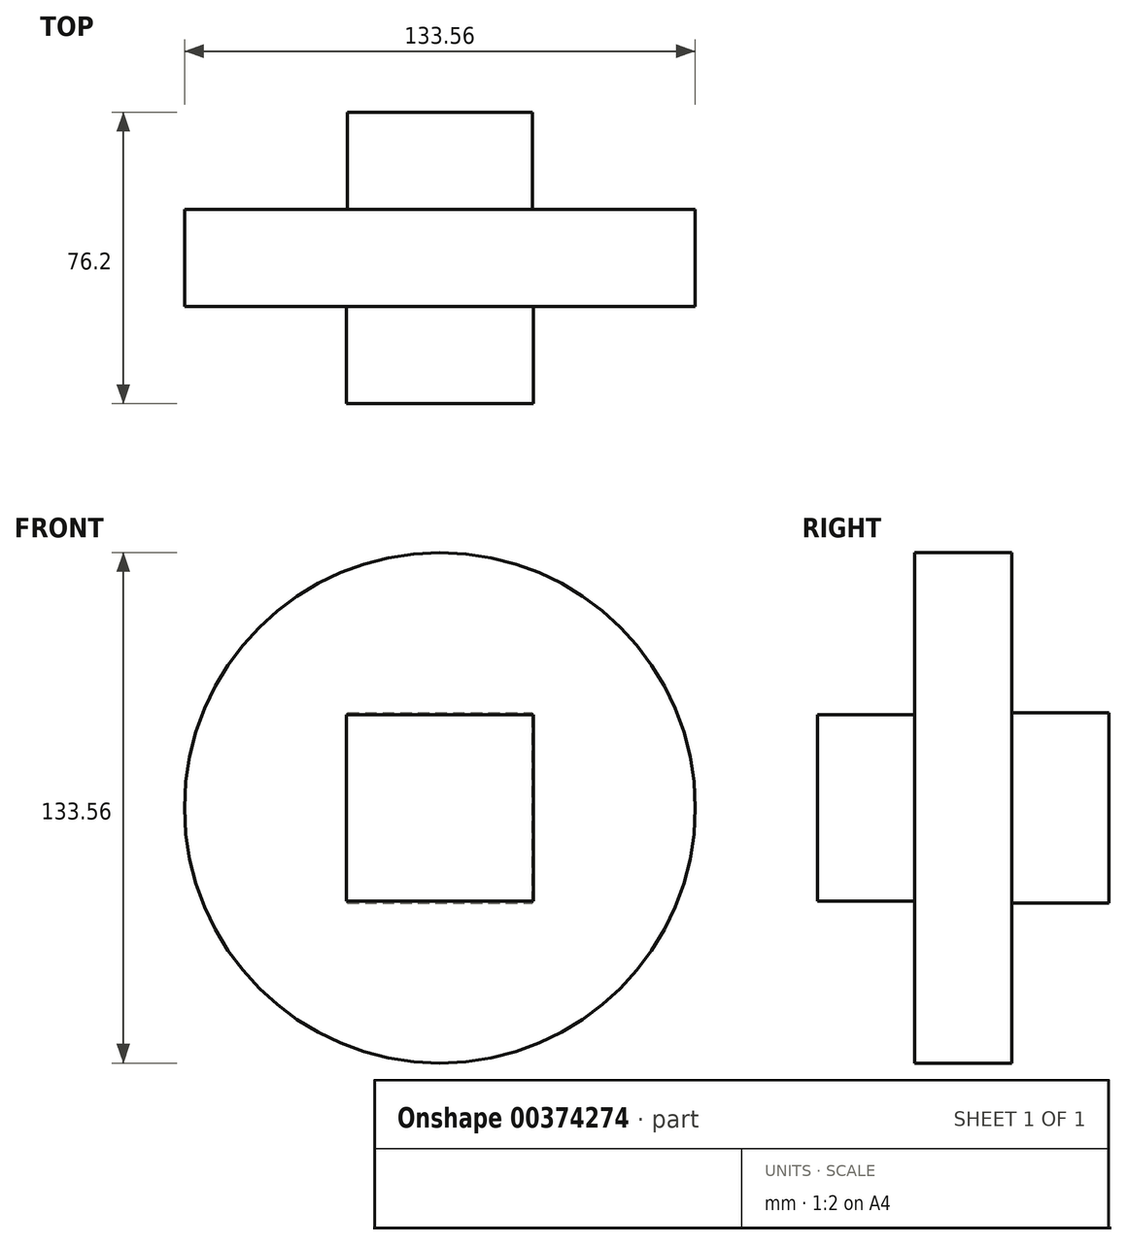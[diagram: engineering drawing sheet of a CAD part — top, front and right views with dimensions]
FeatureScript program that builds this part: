
annotation { "Feature Type Name" : "Feature", "Feature Type Description" : "" }
export const myFeature = defineFeature(function(context is Context, id is Id, definition is map)
    precondition{}
    {
        {
            var Q0;
            Q0=qCreatedBy(makeId("Front.planeOp"),FACE);
            var sketch = newSketch(context, id + "F0", { "sketchPlane" : qUnion([Q0])});
            skCircle(sketch, "E0", {"center": v(0, 0) * mm, "radius": 66.78 * mm});
            skLineSegment(sketch, "E1", {"start": v(0, 66.78) * mm, "end": v(-52.44, -41.35) * mm});
            skLineSegment(sketch, "E2", {"start": v(-52.44, -41.35) * mm, "end": v(0, 66.78) * mm});
            skLineSegment(sketch, "E3", {"start": v(0, 66.78) * mm, "end": v(51.62, -42.36) * mm});
            skLineSegment(sketch, "E4", {"start": v(51.62, -42.36) * mm, "end": v(-52.44, -41.35) * mm});
            skSolve(sketch);
        }
        {
            var Q0;
            Q0=qSketchRegion(id+"F0",true);
            extrude(context, id + "F1", {"entities" : qUnion([Q0]), "depth" : 25.4 * mm});
        }
        {
            var Q0;
            Q0=qCreatedBy(makeId("Front.planeOp"),FACE);
            var sketch = newSketch(context, id + "F2", { "sketchPlane" : qUnion([Q0])});
            skCircle(sketch, "E5", {"center": v(0, 0) * mm, "radius": 18.33 * mm});
            skCircle(sketch, "E6", {"center": v(0, 0) * mm, "radius": 35.86 * mm});
            skSolve(sketch);
        }
        {
            var Q0;
            Q0=qSketchRegion(id+"F2",true);
            extrude(context, id + "F3", {"entities" : qUnion([Q0]), "operationType" : NewBodyOperationType.REMOVE, "oppositeDirection" : true, "depth" : 25.4 * mm});
        }
        {
            var Q0;
            Q0=makeQuery(id+"F1.opExtrude","CAP_FACE",FACE,{"disambiguationData":[OSD([sQuery(id+"F0.wireOp",EDGE,"E0")])],"isStart":false});
            var sketch = newSketch(context, id + "F4", { "sketchPlane" : qUnion([Q0])});
            skLineSegment(sketch, "E7.bottom", {"start": v(24.42, -24.37) * mm, "end": v(-24.42, -24.37) * mm});
            skLineSegment(sketch, "E7.top", {"start": v(24.42, 24.37) * mm, "end": v(-24.42, 24.37) * mm});
            skLineSegment(sketch, "E7.left", {"start": v(24.42, -24.37) * mm, "end": v(24.42, 24.37) * mm});
            skLineSegment(sketch, "E7.right", {"start": v(-24.42, -24.37) * mm, "end": v(-24.42, 24.37) * mm});
            skPoint(sketch, "E7.middle", {"position": v(0, 0) * mm});
            skSolve(sketch);
        }
        {
            var Q0;
            Q0=makeQuery(id+"F4.imprint","IMPRINT",FACE,{"disambiguationData":[TD([[makeQuery(id+"F4.imprint","IMPRINT",EDGE,{"derivedFrom":sQuery(id+"F4.wireOp",EDGE,"E7.bottom")}),-1.0]])]});
            extrude(context, id + "F5", {"entities" : qUnion([Q0]), "operationType" : NewBodyOperationType.ADD, "depth" : 25.4 * mm});
        }
        {
            var Q0;
            Q0=makeQuery(id+"F1.opExtrude","CAP_FACE",FACE,{"disambiguationData":[OSD([sQuery(id+"F0.wireOp",EDGE,"E0")])],"isStart":true});
            var sketch = newSketch(context, id + "F6", { "sketchPlane" : qUnion([Q0])});
            skLineSegment(sketch, "E8.bottom", {"start": v(24.15, -24.9) * mm, "end": v(-24.15, -24.9) * mm});
            skLineSegment(sketch, "E8.top", {"start": v(24.15, 24.9) * mm, "end": v(-24.15, 24.9) * mm});
            skLineSegment(sketch, "E8.left", {"start": v(24.15, -24.9) * mm, "end": v(24.15, 24.9) * mm});
            skLineSegment(sketch, "E8.right", {"start": v(-24.15, -24.9) * mm, "end": v(-24.15, 24.9) * mm});
            skPoint(sketch, "E8.middle", {"position": v(0, 0) * mm});
            skSolve(sketch);
        }
        {
            var Q0;
            Q0=makeQuery(id+"F6.imprint","IMPRINT",FACE,{"disambiguationData":[TD([[makeQuery(id+"F6.imprint","IMPRINT",EDGE,{"derivedFrom":sQuery(id+"F6.wireOp",EDGE,"E8.bottom")}),-1.0]])]});
            extrude(context, id + "F7", {"entities" : qUnion([Q0]), "operationType" : NewBodyOperationType.ADD, "depth" : 25.4 * mm});
        }
    });
